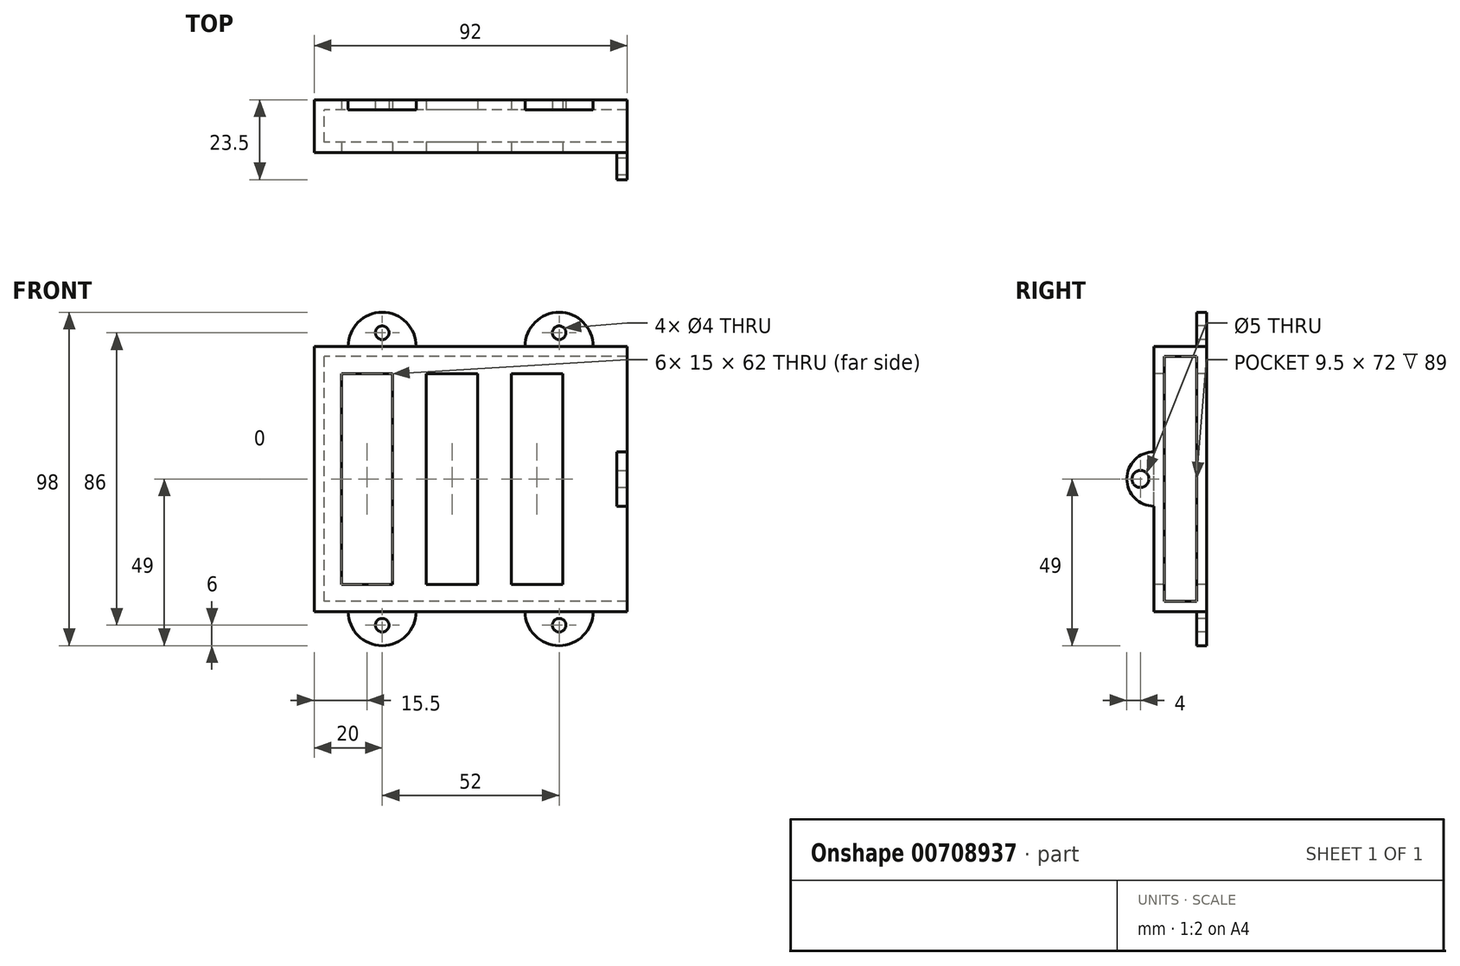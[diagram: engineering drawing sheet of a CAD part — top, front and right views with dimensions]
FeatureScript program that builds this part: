
annotation { "Feature Type Name" : "Feature", "Feature Type Description" : "" }
export const myFeature = defineFeature(function(context is Context, id is Id, definition is map)
    precondition{}
    {
        {
            var Q0;
            Q0=qCreatedBy(makeId("Front.planeOp"),FACE);
            var sketch = newSketch(context, id + "F0", { "sketchPlane" : qUnion([Q0])});
            skLineSegment(sketch, "E0.bottom", {"start": v(0, 0) * mm, "end": v(-92, 0) * mm});
            skLineSegment(sketch, "E0.top", {"start": v(0, 78) * mm, "end": v(-92, 78) * mm});
            skLineSegment(sketch, "E0.left", {"start": v(0, 0) * mm, "end": v(0, 78) * mm});
            skLineSegment(sketch, "E0.right", {"start": v(-92, 0) * mm, "end": v(-92, 78) * mm});
            skSolve(sketch);
        }
        {
            var Q0;
            Q0 = qSketchRegion(id + "F0", true);
            extrude(context, id + "F1", {"entities" : qUnion([Q0]), "depth" : 15.5 * mm, "offsetDistance" : 25 * mm});
        }
        {
            var Q0;
            Q0=makeQuery(id+"F1.opExtrude","SWEPT_FACE",FACE,{"disambiguationData":[OSD([sQuery(id+"F0.wireOp",EDGE,"E0.left")])]});
            shell(context, id + "F2", {"entities" : qUnion([Q0]), "thickness" : 3 * mm});
        }
        {
            var Q0;
            Q0=makeQuery(id+"F1.opExtrude","CAP_FACE",FACE,{"disambiguationData":[OSD([sQuery(id+"F0.wireOp",EDGE,"E0.bottom"),sQuery(id+"F0.wireOp",EDGE,"E0.top"),sQuery(id+"F0.wireOp",EDGE,"E0.left"),sQuery(id+"F0.wireOp",EDGE,"E0.right")])],"isStart":true});
            var sketch = newSketch(context, id + "F3", { "sketchPlane" : qUnion([Q0])});
            skArc(sketch, "E1", {"start": v(82, 78) * mm, "mid": v(72, 88) * mm, "end": v(62, 78) * mm});
            skArc(sketch, "E2", {"start": v(62, 0) * mm, "mid": v(72, -10) * mm, "end": v(82, 0) * mm});
            skArc(sketch, "E3", {"start": v(10, 0) * mm, "mid": v(20, -10) * mm, "end": v(30, 0) * mm});
            skArc(sketch, "E4", {"start": v(30, 78) * mm, "mid": v(20, 88) * mm, "end": v(10, 78) * mm});
            skSolve(sketch);
        }
        {
            var Q0;
            {var subQ0=sQuery(id+"F3.wireOp",EDGE,"E1");Q0=makeQuery(id+"F3.imprint","IMPRINT",FACE,{"disambiguationData":[TD([[makeQuery(id+"F3.imprint","IMPRINT",EDGE,{"derivedFrom":subQ0}),1.0]])]});}
            var Q1;
            {var subQ0=sQuery(id+"F3.wireOp",EDGE,"E2");Q1=makeQuery(id+"F3.imprint","IMPRINT",FACE,{"disambiguationData":[TD([[makeQuery(id+"F3.imprint","IMPRINT",EDGE,{"derivedFrom":subQ0}),1.0]])]});}
            var Q2;
            {var subQ0=sQuery(id+"F3.wireOp",EDGE,"v753D2S2-Qtyg-mQ0d-uK0F-UdB854YgqHTW");Q2=makeQuery(id+"F3.imprint","IMPRINT",FACE,{"disambiguationData":[TD([[makeQuery(id+"F3.imprint","IMPRINT",EDGE,{"derivedFrom":subQ0}),1.0]])]});}
            var Q3;
            {var subQ0=sQuery(id+"F3.wireOp",EDGE,"E4");Q3=makeQuery(id+"F3.imprint","IMPRINT",FACE,{"disambiguationData":[TD([[makeQuery(id+"F3.imprint","IMPRINT",EDGE,{"derivedFrom":subQ0}),1.0]])]});}
            var Q4;
            {var subQ0=sQuery(id+"F3.wireOp",EDGE,"E3");Q4=makeQuery(id+"F3.imprint","IMPRINT",FACE,{"disambiguationData":[TD([[makeQuery(id+"F3.imprint","IMPRINT",EDGE,{"derivedFrom":subQ0}),1.0]])]});}
            extrude(context, id + "F4", {"entities" : qUnion([Q0, Q1, Q2, Q3, Q4]), "operationType" : NewBodyOperationType.ADD, "oppositeDirection" : true, "depth" : 3 * mm, "offsetDistance" : 25 * mm});
        }
        {
            var Q0;
            Q0=makeQuery(id+"F4.opExtrude","CAP_FACE",FACE,{"disambiguationData":[OSD([sQuery(id+"F0.wireOp",EDGE,"E0.top"),sQuery(id+"F3.wireOp",EDGE,"E1")])],"isStart":false});
            var sketch = newSketch(context, id + "F5", { "sketchPlane" : qUnion([Q0])});
            skCircle(sketch, "E5", {"center": v(-72, 82) * mm, "radius": 2 * mm});
            skCircle(sketch, "E6", {"center": v(-72, -4) * mm, "radius": 2 * mm});
            skPoint(sketch, "E7", {"position": v(-72, 78) * mm});
            skCircle(sketch, "E8", {"center": v(-20, 82) * mm, "radius": 2 * mm});
            skCircle(sketch, "E9", {"center": v(-20, -4) * mm, "radius": 2 * mm});
            skSolve(sketch);
        }
        {
            var Q0;
            Q0 = qSketchRegion(id + "F5", true);
            extrude(context, id + "F6", {"entities" : qUnion([Q0]), "operationType" : NewBodyOperationType.REMOVE, "oppositeDirection" : true, "depth" : 25 * mm, "offsetDistance" : 25 * mm});
        }
        {
            var Q0;
            Q0=makeQuery(id+"F1.opExtrude","CAP_FACE",FACE,{"disambiguationData":[OSD([sQuery(id+"F0.wireOp",EDGE,"E0.bottom"),sQuery(id+"F0.wireOp",EDGE,"E0.top"),sQuery(id+"F0.wireOp",EDGE,"E0.left"),sQuery(id+"F0.wireOp",EDGE,"E0.right")])],"isStart":false});
            var sketch = newSketch(context, id + "F7", { "sketchPlane" : qUnion([Q0])});
            skLineSegment(sketch, "E10.bottom", {"start": v(-69, 8) * mm, "end": v(-84, 8) * mm});
            skLineSegment(sketch, "E10.top", {"start": v(-69, 70) * mm, "end": v(-84, 70) * mm});
            skLineSegment(sketch, "E10.left", {"start": v(-69, 8) * mm, "end": v(-69, 70) * mm});
            skLineSegment(sketch, "E10.right", {"start": v(-84, 8) * mm, "end": v(-84, 70) * mm});
            skLineSegment(sketch, "E11.1.0.0", {"start": v(-44, 8) * mm, "end": v(-44, 70) * mm});
            skLineSegment(sketch, "E11.1.0.1", {"start": v(-59, 8) * mm, "end": v(-59, 70) * mm});
            skLineSegment(sketch, "E11.1.0.2", {"start": v(-44, 70) * mm, "end": v(-59, 70) * mm});
            skLineSegment(sketch, "E11.1.0.3", {"start": v(-44, 8) * mm, "end": v(-59, 8) * mm});
            skLineSegment(sketch, "E11.2.0.0", {"start": v(-19, 8) * mm, "end": v(-19, 70) * mm});
            skLineSegment(sketch, "E11.2.0.1", {"start": v(-34, 8) * mm, "end": v(-34, 70) * mm});
            skLineSegment(sketch, "E11.2.0.2", {"start": v(-19, 70) * mm, "end": v(-34, 70) * mm});
            skLineSegment(sketch, "E11.2.0.3", {"start": v(-19, 8) * mm, "end": v(-34, 8) * mm});
            skLineSegment(sketch, "E11.direction1", {"start": v(-69, 8) * mm, "end": v(-44, 8) * mm, "construction": true});
            skSolve(sketch);
        }
        {
            var Q0;
            Q0 = qSketchRegion(id + "F7", true);
            extrude(context, id + "F8", {"entities" : qUnion([Q0]), "operationType" : NewBodyOperationType.REMOVE, "oppositeDirection" : true, "depth" : 25 * mm, "offsetDistance" : 25 * mm});
        }
        {
            var Q0;
            Q0=makeQuery(id+"F1.opExtrude","SWEPT_FACE",FACE,{"disambiguationData":[OSD([sQuery(id+"F0.wireOp",EDGE,"E0.left")])]});
            var sketch = newSketch(context, id + "F9", { "sketchPlane" : qUnion([Q0])});
            skArc(sketch, "E12", {"start": v(-15.5, 47) * mm, "mid": v(-23.5, 39) * mm, "end": v(-15.5, 31) * mm});
            skLineSegment(sketch, "E13", {"start": v(-15.5, 31) * mm, "end": v(-15.5, 47) * mm});
            skSolve(sketch);
        }
        {
            var Q0;
            Q0 = qSketchRegion(id + "F9", true);
            extrude(context, id + "F10", {"entities" : qUnion([Q0]), "operationType" : NewBodyOperationType.ADD, "oppositeDirection" : true, "depth" : 3 * mm, "offsetDistance" : 25 * mm});
        }
        {
            var Q0;
            Q0=makeQuery(id+"F10.boolean.opBoolean","MERGE",FACE,{"derivedFrom":[makeQuery(id+"F1.opExtrude","SWEPT_FACE",FACE,{"disambiguationData":[OSD([sQuery(id+"F0.wireOp",EDGE,"E0.left")])]}),makeQuery(id+"F10.opExtrude","CAP_FACE",FACE,{"disambiguationData":[OSD([sQuery(id+"F9.wireOp",EDGE,"E12"),sQuery(id+"F9.wireOp",EDGE,"E13")])],"isStart":true})]});
            var sketch = newSketch(context, id + "F11", { "sketchPlane" : qUnion([Q0])});
            skCircle(sketch, "E14", {"center": v(-19.5, 39) * mm, "radius": 2.5 * mm});
            skPoint(sketch, "E15", {"position": v(-12.5, 39) * mm});
            skSolve(sketch);
        }
        {
            var Q0;
            Q0 = qSketchRegion(id + "F11", true);
            extrude(context, id + "F12", {"entities" : qUnion([Q0]), "operationType" : NewBodyOperationType.REMOVE, "oppositeDirection" : true, "depth" : 5 * mm, "offsetDistance" : 25 * mm});
        }
    });
